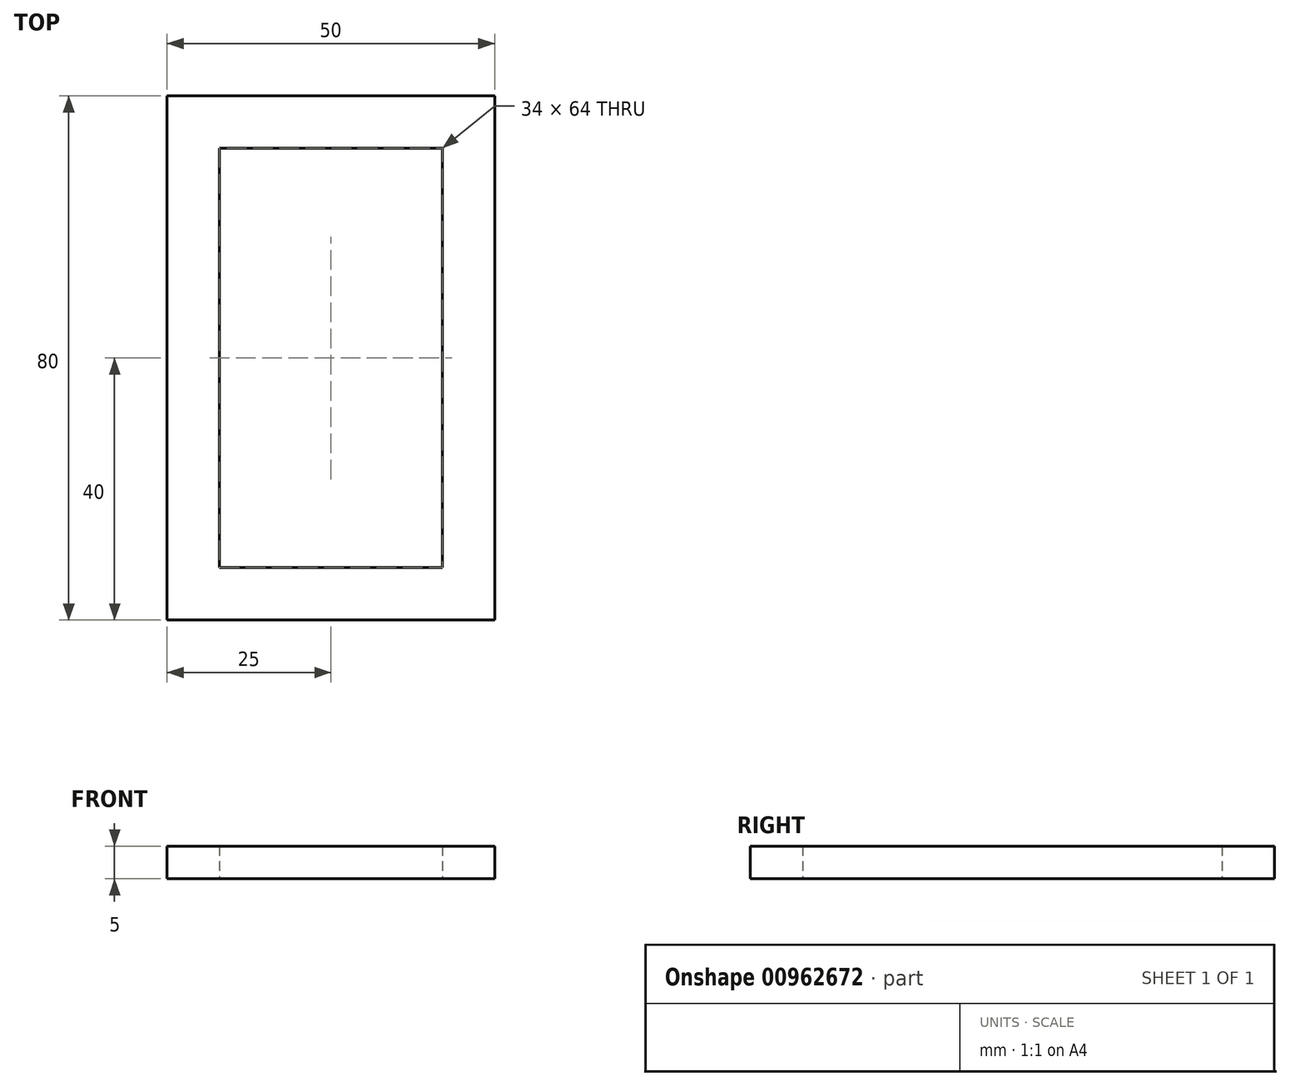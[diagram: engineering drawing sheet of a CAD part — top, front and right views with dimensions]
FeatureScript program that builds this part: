
annotation { "Feature Type Name" : "Feature", "Feature Type Description" : "" }
export const myFeature = defineFeature(function(context is Context, id is Id, definition is map)
    precondition{}
    {
        {
            var Q0;
            Q0=qCreatedBy(makeId("Top.planeOp"),FACE);
            var sketch = newSketch(context, id + "F0", { "sketchPlane" : qUnion([Q0])});
            skLineSegment(sketch, "E0", {"start": v(0, 0) * mm, "end": v(50, 0) * mm});
            skLineSegment(sketch, "E1", {"start": v(50, 0) * mm, "end": v(50, -80) * mm});
            skLineSegment(sketch, "E2", {"start": v(0, 0) * mm, "end": v(0, -80) * mm});
            skLineSegment(sketch, "E3", {"start": v(50, -80) * mm, "end": v(0, -80) * mm});
            skLineSegment(sketch, "E4", {"start": v(8, -8) * mm, "end": v(42, -8) * mm});
            skLineSegment(sketch, "E5", {"start": v(42, -8) * mm, "end": v(42, -72) * mm});
            skLineSegment(sketch, "E6", {"start": v(8, -8) * mm, "end": v(8, -72) * mm});
            skLineSegment(sketch, "E7", {"start": v(42, -72) * mm, "end": v(8, -72) * mm});
            skLineSegment(sketch, "E8", {"start": v(8, -8) * mm, "end": v(0, -8) * mm, "construction": true});
            skLineSegment(sketch, "E9", {"start": v(42, -8) * mm, "end": v(50, -8) * mm, "construction": true});
            skLineSegment(sketch, "E10", {"start": v(42, -72) * mm, "end": v(50, -72) * mm, "construction": true});
            skLineSegment(sketch, "E11", {"start": v(8, -72) * mm, "end": v(0, -72) * mm, "construction": true});
            skLineSegment(sketch, "E12", {"start": v(8, 0) * mm, "end": v(8, -8) * mm, "construction": true});
            skLineSegment(sketch, "E13", {"start": v(42, 0) * mm, "end": v(42, -8) * mm, "construction": true});
            skLineSegment(sketch, "E14", {"start": v(42, -72) * mm, "end": v(42, -80) * mm, "construction": true});
            skLineSegment(sketch, "E15", {"start": v(8, -72) * mm, "end": v(8, -80) * mm, "construction": true});
            skSolve(sketch);
        }
        {
            var Q0;
            Q0 = qSketchRegion(id + "F0", true);
            extrude(context, id + "F1", {"entities" : qUnion([Q0]), "depth" : 5 * mm, "offsetDistance" : 25.4 * mm});
        }
    });
